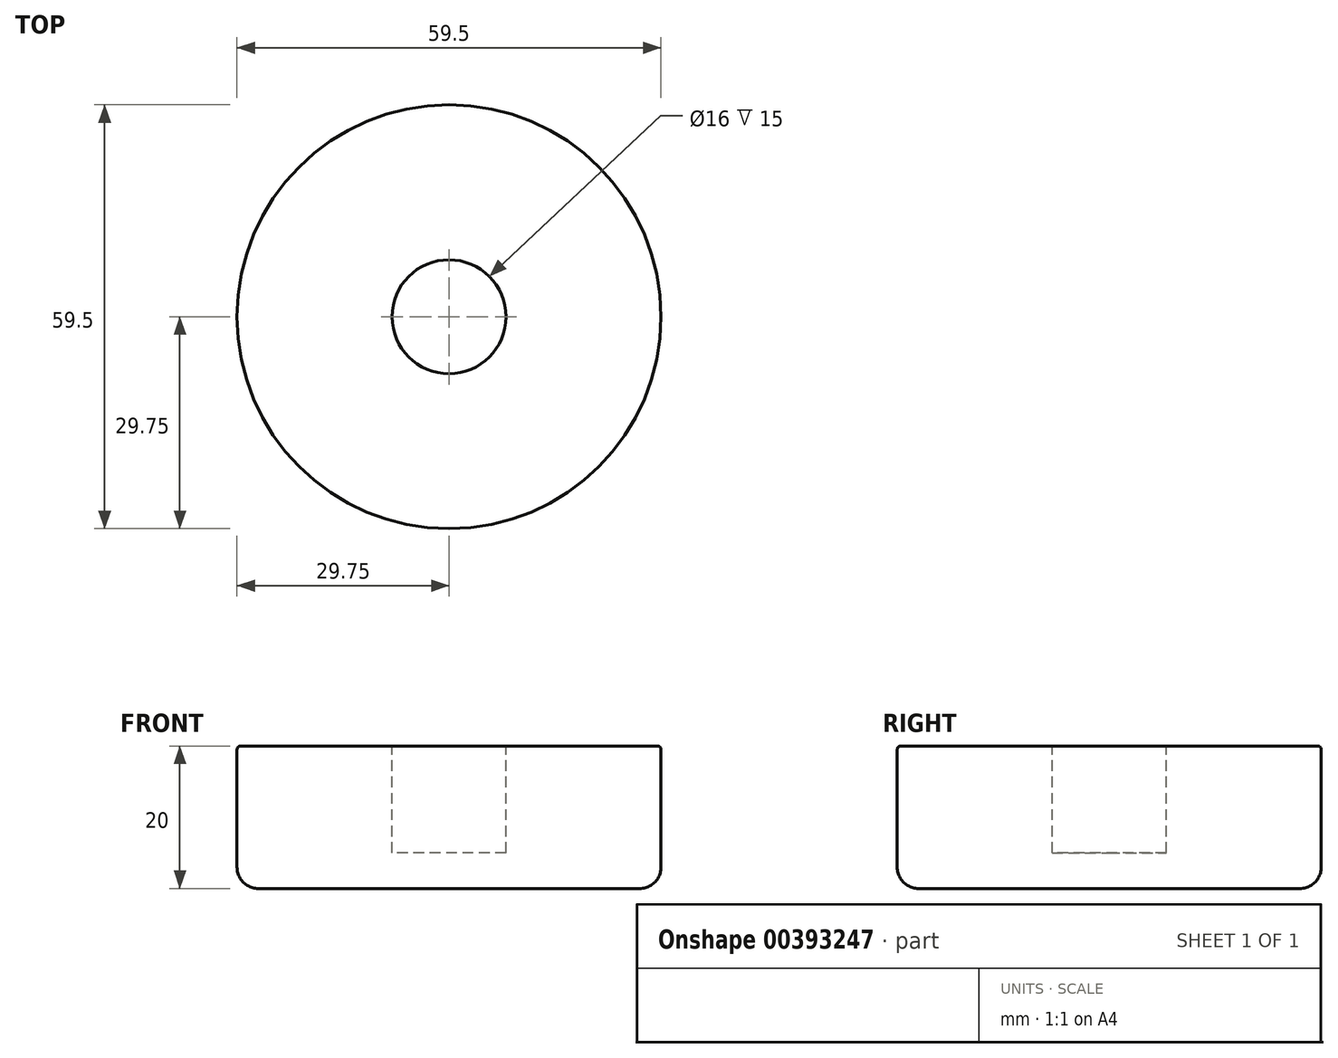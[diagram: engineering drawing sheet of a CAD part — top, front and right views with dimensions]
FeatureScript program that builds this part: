
annotation { "Feature Type Name" : "Feature", "Feature Type Description" : "" }
export const myFeature = defineFeature(function(context is Context, id is Id, definition is map)
    precondition{}
    {
        {
            var Q0;
            Q0=qCreatedBy(makeId("Top.planeOp"),FACE);
            var sketch = newSketch(context, id + "F0", { "sketchPlane" : qUnion([Q0])});
            skCircle(sketch, "E0", {"center": v(0, 0) * mm, "radius": 29.75 * mm});
            skSolve(sketch);
        }
        {
            var Q0;
            Q0 = qSketchRegion(id + "F0", true);
            extrude(context, id + "F1", {"entities" : qUnion([Q0]), "depth" : 20 * mm});
        }
        {
            var Q0;
            Q0=makeQuery(id+"F1.opExtrude","CAP_FACE",FACE,{"disambiguationData":[OSD([sQuery(id+"F0.wireOp",EDGE,"E0")])],"isStart":false});
            var sketch = newSketch(context, id + "F2", { "sketchPlane" : qUnion([Q0])});
            skCircle(sketch, "E1", {"center": v(0, 0) * mm, "radius": 8 * mm});
            skSolve(sketch);
        }
        {
            var Q0;
            Q0 = qSketchRegion(id + "F2", true);
            extrude(context, id + "F3", {"entities" : qUnion([Q0]), "operationType" : NewBodyOperationType.REMOVE, "oppositeDirection" : true, "depth" : 15 * mm});
        }
        {
            var Q0;
            Q0=makeQuery(id+"F1.opExtrude","CAP_EDGE",EDGE,{"disambiguationData":[OSD([sQuery(id+"F0.wireOp",EDGE,"E0")])],"isStart":false});
            fillet(context, id + "F4", {"entities" : qUnion([Q0]), "radius" : 0.5 * mm, "tangentPropagation" : true, "allowEdgeOverflow" : false});
        }
        {
            var Q0;
            Q0=makeQuery(id+"F1.opExtrude","CAP_EDGE",EDGE,{"disambiguationData":[OSD([sQuery(id+"F0.wireOp",EDGE,"E0")])],"isStart":true});
            fillet(context, id + "F5", {"entities" : qUnion([Q0]), "radius" : 3 * mm, "tangentPropagation" : true, "allowEdgeOverflow" : false});
        }
    });
